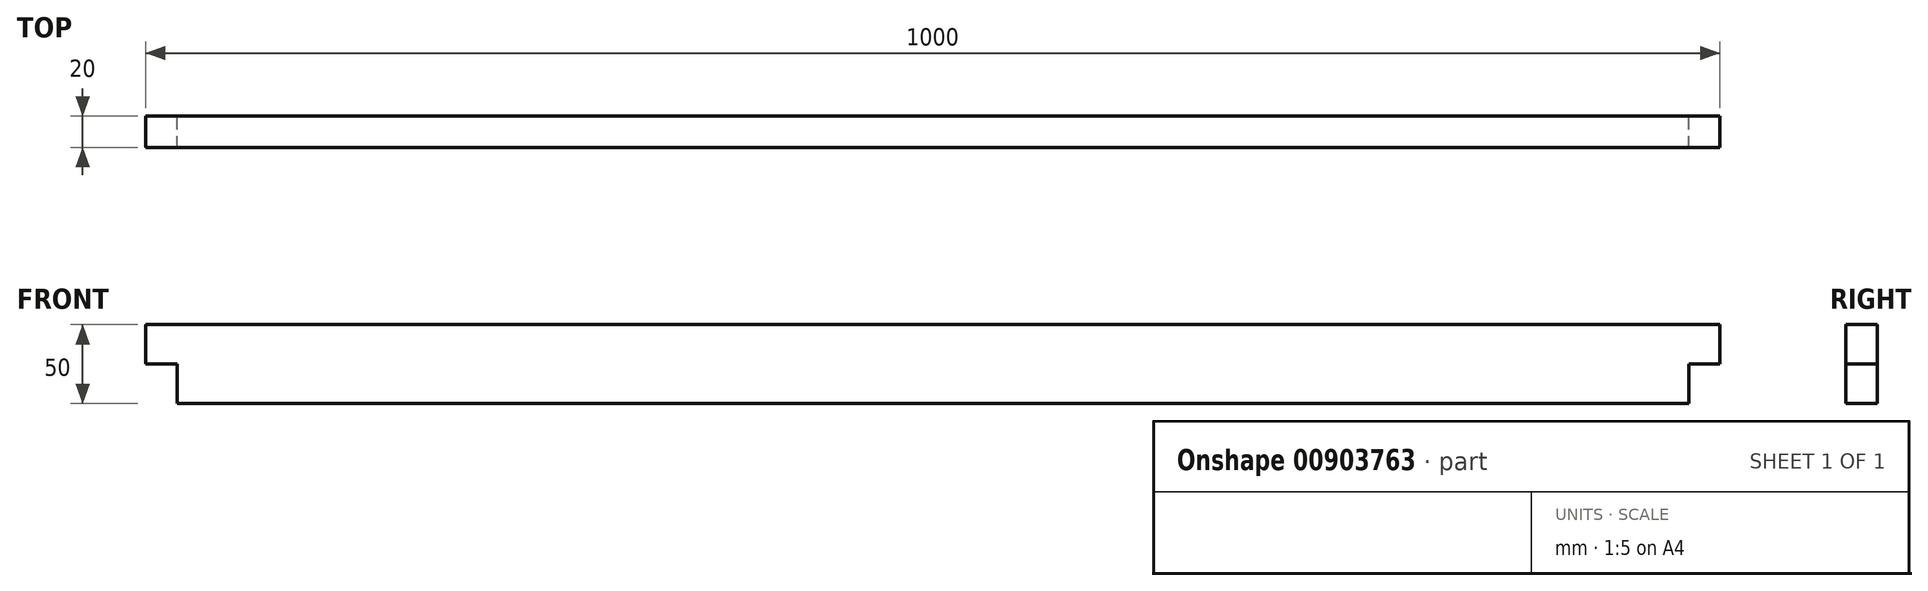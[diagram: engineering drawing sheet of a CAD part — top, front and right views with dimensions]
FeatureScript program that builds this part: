
annotation { "Feature Type Name" : "Feature", "Feature Type Description" : "" }
export const myFeature = defineFeature(function(context is Context, id is Id, definition is map)
    precondition{}
    {
        {
            var Q0;
            Q0=qCreatedBy(makeId("Front.planeOp"),FACE);
            var sketch = newSketch(context, id + "F0", { "sketchPlane" : qUnion([Q0])});
            skLineSegment(sketch, "E0.bottom", {"start": v(-500, 25) * mm, "end": v(500, 25) * mm});
            skLineSegment(sketch, "E0.top", {"start": v(-500, -25) * mm, "end": v(500, -25) * mm});
            skLineSegment(sketch, "E0.left", {"start": v(-500, 25) * mm, "end": v(-500, -25) * mm});
            skLineSegment(sketch, "E0.right", {"start": v(500, 25) * mm, "end": v(500, -25) * mm});
            skLineSegment(sketch, "E1.bottom", {"start": v(-500, 0) * mm, "end": v(-480, 0) * mm});
            skLineSegment(sketch, "E1.top", {"start": v(-500, -25) * mm, "end": v(-480, -25) * mm});
            skLineSegment(sketch, "E1.left", {"start": v(-500, 0) * mm, "end": v(-500, -25) * mm});
            skLineSegment(sketch, "E1.right", {"start": v(-480, 0) * mm, "end": v(-480, -25) * mm});
            skLineSegment(sketch, "E2.MirrorCS", {"start": v(480, 0) * mm, "end": v(480, -25) * mm});
            skLineSegment(sketch, "E3.MirrorCS", {"start": v(500, 0) * mm, "end": v(480, 0) * mm});
            skSolve(sketch);
        }
        {
            var Q0;
            Q0=makeQuery(id+"F0.imprint","IMPRINT",FACE,{"disambiguationData":[TD([[makeQuery(id+"F0.imprint","IMPRINT",EDGE,{"derivedFrom":sQuery(id+"F0.wireOp",EDGE,"E0.bottom")}),-1.0]])]});
            extrude(context, id + "F1", {"entities" : qUnion([Q0]), "depth" : 20 * mm, "offsetDistance" : 25 * mm});
        }
    });
